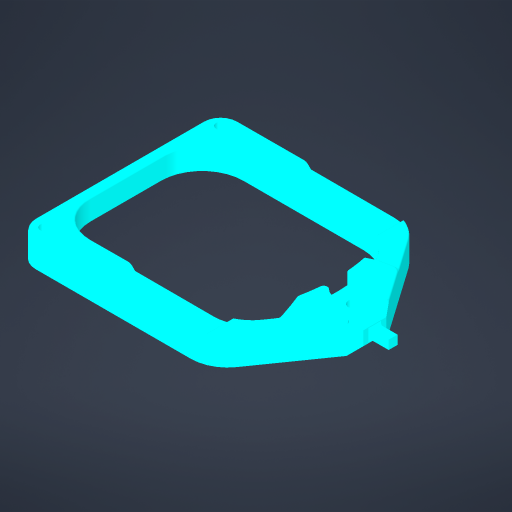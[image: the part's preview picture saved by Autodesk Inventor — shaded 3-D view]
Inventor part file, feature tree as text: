
AUTODESK INVENTOR PART (.ipt)
format: ipt  version: 2023.4 (Build 274418000, 418)  size: 573,952 bytes
history: native  units: mm
features: projected_geometry x8, sketch x7, extrude x7, reference x7, chamfer x5, fillet x4, other x4, plane x2
ambient origin geometry x8: Origin, YZ Plane, XZ Plane, XY Plane, X Axis, Y Axis, Z Axis, Center Point
bodies: Solid1 (feature_tree)
feature tree (44):
  sketch  "Sketch1"  dims[d0=15.0mm d1=9.599311mm]
  plane  "Work Plane1"
  plane  "Work Plane2"
  extrude  "Extrusion1"  Depth=9.599311mm
  chamfer  "Chamfer1"  Distance=10.0mm
  extrude  "Extrusion2"  Depth=0.0125mm
  extrude  "Extrusion3"  Depth=50.0mm TaperAngle=0.0deg
  fillet  "Fillet1"  Radius=15.0mm
  fillet  "Fillet2"  Radius=7.5mm
  extrude  "Extrusion4"  Depth=52.5mm
  chamfer  "Chamfer2"  Distance=50.0mm
  extrude  "Extrusion5"  Depth=5.0mm
  extrude  "Extrusion6"  Depth=0.875mm
  extrude  "Extrusion7"  Depth=0.875mm
  chamfer  "Chamfer3"  Distance=1.25mm
  chamfer  "Chamfer4"  Distance=10.0mm
  chamfer  "Chamfer5"  Distance=1.25mm Angle=45.0deg
  fillet  "Fillet3"  Radius=4.0mm
  fillet  "Fillet4"  Radius=2.875mm
  reference  "Reference1"
  reference  "Reference2"
  sketch  "Sketch2"  dims[d2=5.0mm d3=10.0mm d4=0.0mm]
  projected_geometry  "Projected Loop1"
  projected_geometry  "Projected Loop2"
  sketch  "Sketch3"  dims[d5=1.875mm d6=2.0mm d7=45.0deg d8=0.0125mm]
  projected_geometry  "Projected Loop3"
  sketch  "Sketch4"  dims[d9=0.0125mm d10=50.0mm d11=0.0mm d12=15.0mm d13=7.5mm]
  projected_geometry  "Projected Loop4"
  reference  "Reference3"
  reference  "Reference4"
  sketch  "Sketch5"  dims[d14=90.0deg d15=52.5mm]
  projected_geometry  "Projected Loop5"
  sketch  "Sketch6"  dims[d16=2.5mm d17=50.0mm d18=0.0mm]
  reference  "Reference5"
  projected_geometry  "Projected Loop6"
  projected_geometry  "Projected Loop7"
  sketch  "Sketch7"  dims[d19=10.0mm d20=5.0mm d21=3.742704mm d22=28.25mm d23=1.25mm d24=10.0mm d25=0.0mm d26=1.25mm d27=2.0mm d28=45.0deg d29=4.0mm d30=2.875mm d31=10.0mm d32=0.0mm d33=1.25mm d34=2.0mm d35=45.0deg d36=0.0675mm d37=3.375mm d38=0.0mm d39=3.375mm d40=2.0mm d41=45.0deg d42=1.0mm d44=5.0mm d45=0.0mm d47=0.5mm d48=2.0mm d49=45.0deg d50=0.875mm d51=0.0375mm]
  projected_geometry  "Projected Loop8"
  reference  "Reference6"
  reference  "Reference7"
  other  "XYZ Stage V5.iam"
  other  "X Stage Body V5:1"
  parser-record x1  (decoder bookkeeping rows leaked as tree rows — omitted from the tree; the rows remain in map.json)
  other  "Z Stage Body New:1"
note: 1 file-system path scrubbed to <path> (originals preserved in map.json)
